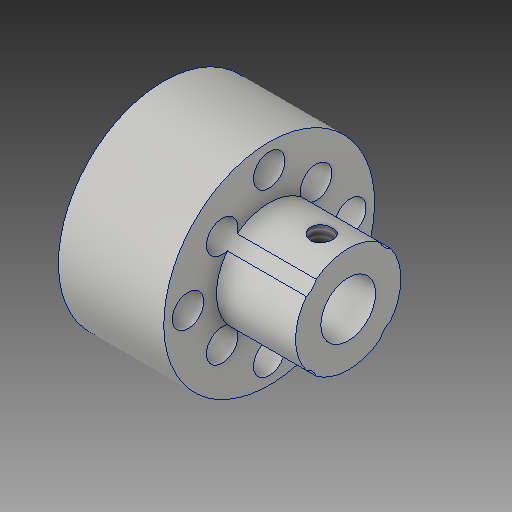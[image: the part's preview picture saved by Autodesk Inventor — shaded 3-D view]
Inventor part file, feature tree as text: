
AUTODESK INVENTOR PART (.ipt)
format: ipt  version: 2017 (Build 210142000, 142)  size: 175,616 bytes
history: native  units: in
note: dims shown in document units (in); Inventor stores cm internally (conversion verified against a paired STEP export)
features: other x3, sketch x3
ambient origin geometry x8: Origin, YZ Plane, XZ Plane, XY Plane, X Axis, Y Axis, Z Axis, Center Point
bodies: Solid1 (feature_tree)
feature tree (6):
  other  "WheelandSprocketComboHub2.ipt"
  other  "Solid1::WheelandSprocketComboHub2.ipt"
  other  "TaggingFeature1"
  sketch  "Sketch1"  dims[d0=0.3937in]
  sketch  "Sketch2"
  sketch  "Sketch5"
